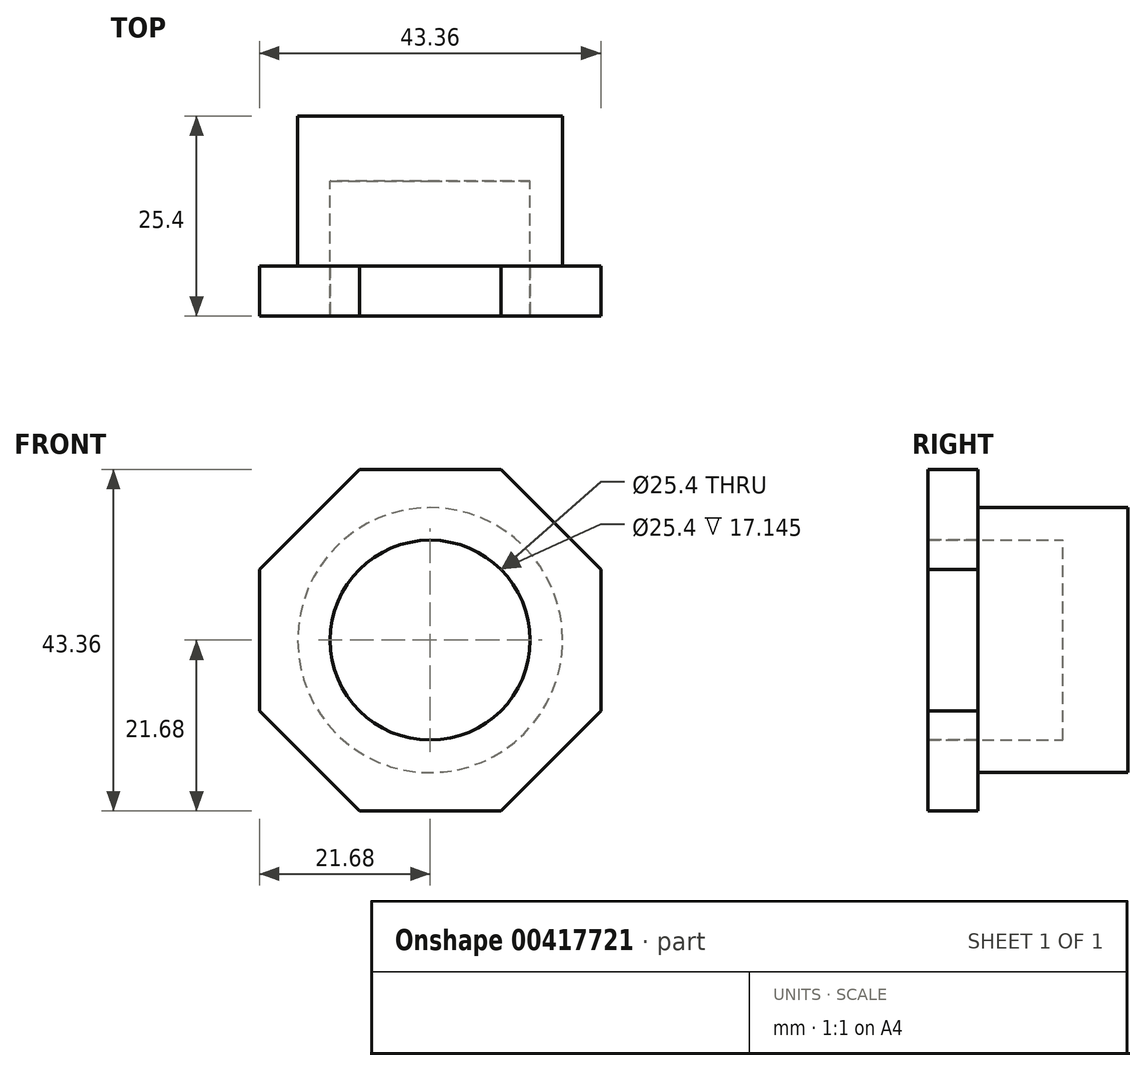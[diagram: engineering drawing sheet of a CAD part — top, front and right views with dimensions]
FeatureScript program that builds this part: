
annotation { "Feature Type Name" : "Feature", "Feature Type Description" : "" }
export const myFeature = defineFeature(function(context is Context, id is Id, definition is map)
    precondition{}
    {
        {
            var Q0;
            Q0=qCreatedBy(makeId("Front.planeOp"),FACE);
            var sketch = newSketch(context, id + "F0", { "sketchPlane" : qUnion([Q0])});
            skCircle(sketch, "E0", {"center": v(0, 0) * mm, "radius": 16.83 * mm});
            skCircle(sketch, "E1", {"center": v(0, 0) * mm, "radius": 12.7 * mm});
            skSolve(sketch);
        }
        {
            var Q0;
            Q0=makeQuery(id+"F0.imprint","IMPRINT",FACE,{"disambiguationData":[TD([[makeQuery(id+"F0.imprint","IMPRINT",EDGE,{"derivedFrom":sQuery(id+"F0.wireOp",EDGE,"E1")}),1.0]])]});
            extrude(context, id + "F1", {"entities" : qUnion([Q0]), "depth" : 8.25 * mm});
        }
        {
            var Q0;
            Q0 = qSketchRegion(id + "F0", true);
            extrude(context, id + "F2", {"entities" : qUnion([Q0]), "operationType" : NewBodyOperationType.ADD, "depth" : 25.4 * mm});
        }
        {
            var Q0;
            Q0=makeQuery(id+"F2.opExtrude","CAP_FACE",FACE,{"disambiguationData":[OSD([sQuery(id+"F0.wireOp",EDGE,"E0"),sQuery(id+"F0.wireOp",EDGE,"E1")])],"isStart":false});
            var sketch = newSketch(context, id + "F3", { "sketchPlane" : qUnion([Q0])});
            skCircle(sketch, "E2.cCircle", {"center": v(0, 0) * mm, "radius": 21.68 * mm, "construction": true});
            skLineSegment(sketch, "E2.0", {"start": v(8.98, -21.68) * mm, "end": v(-8.98, -21.68) * mm});
            skLineSegment(sketch, "E2.1", {"start": v(-8.98, -21.68) * mm, "end": v(-21.68, -8.98) * mm});
            skLineSegment(sketch, "E2.2", {"start": v(-21.68, -8.98) * mm, "end": v(-21.68, 8.98) * mm});
            skLineSegment(sketch, "E2.3", {"start": v(-21.68, 8.98) * mm, "end": v(-8.98, 21.68) * mm});
            skLineSegment(sketch, "E2.4", {"start": v(-8.98, 21.68) * mm, "end": v(8.98, 21.68) * mm});
            skLineSegment(sketch, "E2.5", {"start": v(8.98, 21.68) * mm, "end": v(21.68, 8.98) * mm});
            skLineSegment(sketch, "E2.6", {"start": v(21.68, 8.98) * mm, "end": v(21.68, -8.98) * mm});
            skLineSegment(sketch, "E2.7", {"start": v(21.68, -8.98) * mm, "end": v(8.98, -21.68) * mm});
            skPoint(sketch, "E2.0.midPoint", {"position": v(0, -21.68) * mm});
            skSolve(sketch);
        }
        {
            var Q0;
            Q0=makeQuery(id+"F3.imprint","IMPRINT",FACE,{"disambiguationData":[TD([[makeQuery(id+"F3.imprint","IMPRINT",EDGE,{"derivedFrom":sQuery(id+"F3.wireOp",EDGE,"E2.0")}),-1.0]])]});
            extrude(context, id + "F4", {"entities" : qUnion([Q0]), "oppositeDirection" : true, "depth" : 6.35 * mm});
        }
    });
